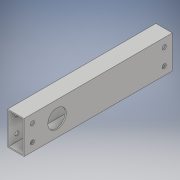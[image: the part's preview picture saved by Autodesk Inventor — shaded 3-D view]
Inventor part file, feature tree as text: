
AUTODESK INVENTOR PART (.ipt)
format: ipt  version: 2018 (Build 220112000, 112)  size: 123,392 bytes
history: native  units: in
note: dims shown in document units (in); Inventor stores cm internally (conversion verified against a paired STEP export)
features: hole x5, extrude x1, shell x1, sketch x1
ambient origin geometry x8: Origin, YZ Plane, XZ Plane, XY Plane, X Axis, Y Axis, Z Axis, Center Point
bodies: Solid1 (feature_tree)
feature tree (8):
  extrude  "Extrusion1"  Depth=2.0in
  shell  "Shell1"  Thickness=9.0in
  hole  "Hole3"  [1 undecoded]
  hole  "Hole4"  [1 undecoded]
  hole  "Hole5"  [1 undecoded]
  hole  "Hole7"  [1 undecoded]
  hole  "Hole8"  [1 undecoded]
  sketch  "Sketch1"  dims[d0=1.0in d1=2.0in d2=9.0in d3=0.0in d4=0.0625in d23=0.5in d24=0.5in d25=0.25in d26=0.75in d27=0.375in d28=0.25in d29=0.5635in d30=1.0in d31=0.8108in d32=0.5in d33=0.5in d34=0.25in d35=0.75in d36=0.375in d37=0.25in d38=0.5635in d39=1.0in d40=0.8108in d41=2.0in d42=1.0in d43=1.125in d44=0.75in d45=0.375in d46=0.25in d47=0.5635in d48=1.0in d49=0.8108in d59=0.5in d60=0.5in d61=0.25in d62=0.75in d63=0.375in d64=0.25in d65=0.5635in d66=1.0in d67=0.8108in d68=0.5in d69=0.5in d70=0.25in d71=0.75in d72=0.375in d73=0.25in d74=0.5635in d75=1.0in d76=0.8108in d50=1.0in d51=1.0in]
note: 5 required parameter values undecoded (feature->parameter linkage not recoverable at this tier; creation-order binding heuristic only, values carry confidence <= 0.55)
